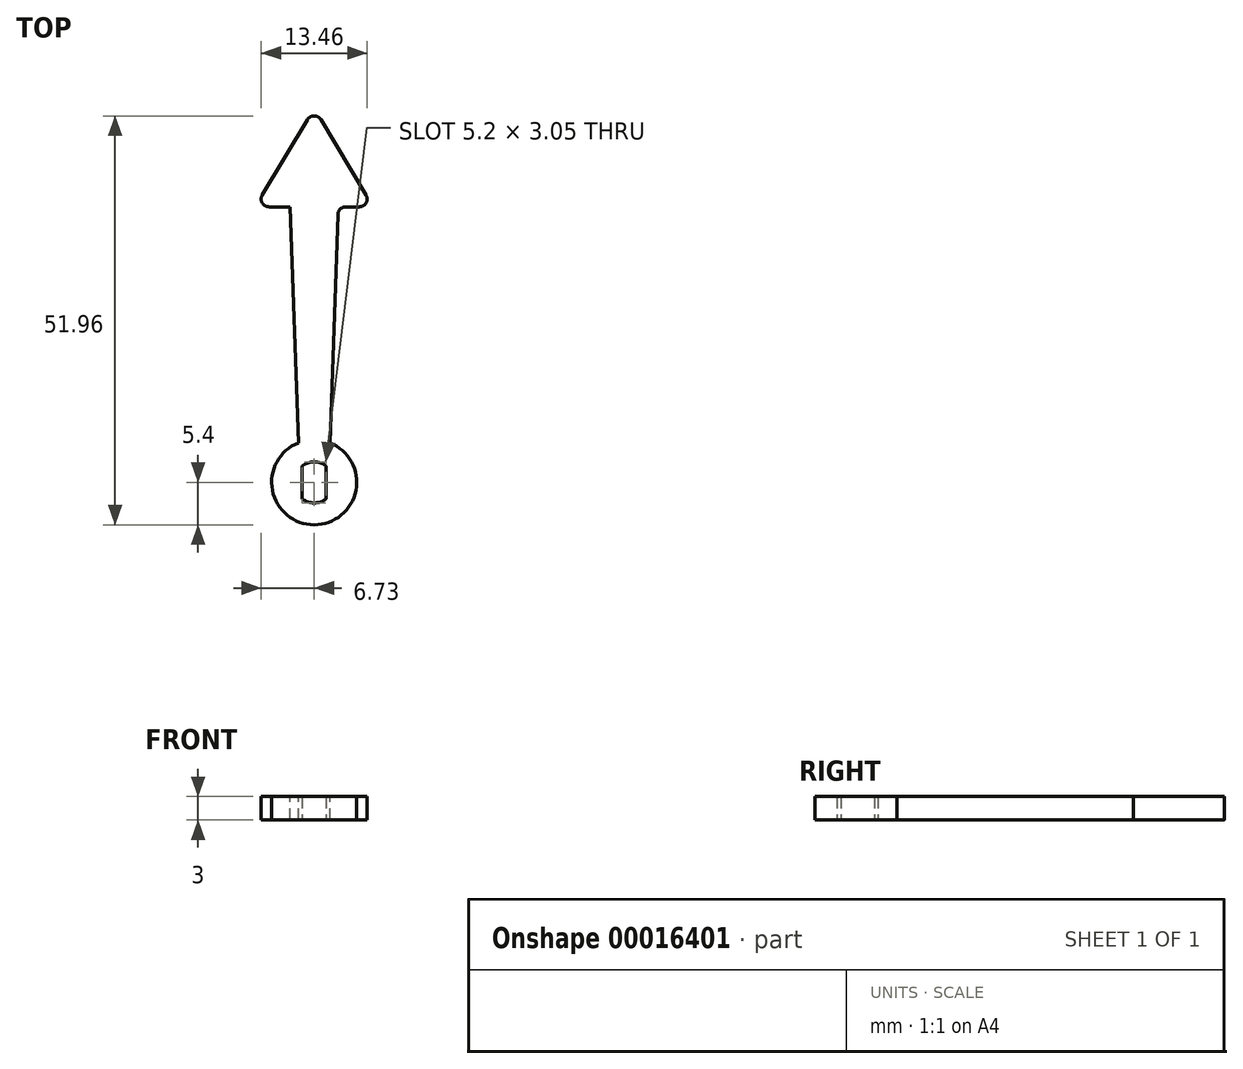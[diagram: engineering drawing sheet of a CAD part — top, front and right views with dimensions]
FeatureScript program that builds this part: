
annotation { "Feature Type Name" : "Feature", "Feature Type Description" : "" }
export const myFeature = defineFeature(function(context is Context, id is Id, definition is map)
    precondition{}
    {
        {
            var Q0;
            Q0=qCreatedBy(makeId("Top.planeOp"),FACE);
            var sketch = newSketch(context, id + "F0", { "sketchPlane" : qUnion([Q0])});
            skCircle(sketch, "E0", {"center": v(0, 0) * mm, "radius": 5.4 * mm});
            skCircle(sketch, "E1", {"center": v(0, 0) * mm, "radius": 2.6 * mm});
            skLineSegment(sketch, "E2", {"start": v(-1.53, 2.1) * mm, "end": v(-1.52, -2.1) * mm});
            skLineSegment(sketch, "E3", {"start": v(1.52, 2.1) * mm, "end": v(1.53, -2.1) * mm});
            skSolve(sketch);
        }
        {
            var Q0;
            Q0 = qSketchRegion(id + "F0", true);
            var Q1;
            {var subQ0=sQuery(id+"F0.wireOp",EDGE,"E3");Q1=makeQuery(id+"F0.imprint","IMPRINT",FACE,{"disambiguationData":[TD([[makeQuery(id+"F0.imprint","IMPRINT",EDGE,{"derivedFrom":subQ0}),1.0]])]});}
            var Q2;
            {var subQ0=sQuery(id+"F0.wireOp",EDGE,"E2");Q2=makeQuery(id+"F0.imprint","IMPRINT",FACE,{"disambiguationData":[TD([[makeQuery(id+"F0.imprint","IMPRINT",EDGE,{"derivedFrom":subQ0}),-1.0]])]});}
            extrude(context, id + "F1", {"entities" : qUnion([Q0, Q1, Q2]), "endBound" : BoundingType.SYMMETRIC, "depth" : 3 * mm});
        }
        {
            var Q0;
            Q0=makeQuery(id+"F1.opExtrude","CAP_FACE",FACE,{"disambiguationData":[OSD([sQuery(id+"F0.wireOp",EDGE,"0dc37ae7-439b-4512-b14e-6b0669575397"),sQuery(id+"F0.wireOp",EDGE,"E0"),sQuery(id+"F0.wireOp",EDGE,"48a892c1-0b3d-49af-834a-82fde92222b2"),sQuery(id+"F0.wireOp",EDGE,"72ea963c-e453-471c-a4fc-8eb423260cf1"),sQuery(id+"F0.wireOp",EDGE,"0ad86a4b-ed37-49b1-82e4-c23b011ab9ce.trimOffspring")])],"isStart":false});
            var sketch = newSketch(context, id + "F2", { "sketchPlane" : qUnion([Q0])});
            skLineSegment(sketch, "E4", {"start": v(0, 0) * mm, "end": v(0, 35) * mm, "construction": true});
            skLineSegment(sketch, "E5", {"start": v(-3.05, 35) * mm, "end": v(3.05, 35) * mm});
            skLineSegment(sketch, "E6", {"start": v(-2, 5.02) * mm, "end": v(2, 5.02) * mm});
            skLineSegment(sketch, "E7", {"start": v(3.05, 35) * mm, "end": v(2, 5.02) * mm});
            skLineSegment(sketch, "E8", {"start": v(-3.05, 35) * mm, "end": v(-2, 5.02) * mm});
            skSolve(sketch);
        }
        {
            var Q0;
            Q0 = qSketchRegion(id + "F2", true);
            var Q1;
            Q1=makeQuery(id+"F1.opExtrude","CAP_FACE",FACE,{"disambiguationData":[OSD([sQuery(id+"F0.wireOp",EDGE,"0dc37ae7-439b-4512-b14e-6b0669575397"),sQuery(id+"F0.wireOp",EDGE,"E0"),sQuery(id+"F0.wireOp",EDGE,"48a892c1-0b3d-49af-834a-82fde92222b2"),sQuery(id+"F0.wireOp",EDGE,"72ea963c-e453-471c-a4fc-8eb423260cf1"),sQuery(id+"F0.wireOp",EDGE,"0ad86a4b-ed37-49b1-82e4-c23b011ab9ce.trimOffspring")])],"isStart":true});
            extrude(context, id + "F3", {"entities" : qUnion([Q0]), "operationType" : NewBodyOperationType.ADD, "endBound" : BoundingType.UP_TO_SURFACE, "oppositeDirection" : true, "endBoundEntityFace" : qUnion([Q1]), "depth" : 25 * mm});
        }
        {
            var Q0;
            Q0=makeQuery(id+"F3.boolean.opBoolean","MERGE",FACE,{"derivedFrom":[makeQuery(id+"F1.opExtrude","CAP_FACE",FACE,{"disambiguationData":[OSD([sQuery(id+"F0.wireOp",EDGE,"0dc37ae7-439b-4512-b14e-6b0669575397"),sQuery(id+"F0.wireOp",EDGE,"E0"),sQuery(id+"F0.wireOp",EDGE,"48a892c1-0b3d-49af-834a-82fde92222b2"),sQuery(id+"F0.wireOp",EDGE,"72ea963c-e453-471c-a4fc-8eb423260cf1"),sQuery(id+"F0.wireOp",EDGE,"0ad86a4b-ed37-49b1-82e4-c23b011ab9ce.trimOffspring")])],"isStart":false}),makeQuery(id+"F3.opExtrude","CAP_FACE",FACE,{"disambiguationData":[OSD([sQuery(id+"F2.wireOp",EDGE,"E5"),sQuery(id+"F2.wireOp",EDGE,"E6"),sQuery(id+"F2.wireOp",EDGE,"E7"),sQuery(id+"F2.wireOp",EDGE,"E8")])],"isStart":true})]});
            var sketch = newSketch(context, id + "F4", { "sketchPlane" : qUnion([Q0])});
            skLineSegment(sketch, "E9", {"start": v(0, 35) * mm, "end": v(0, 47.5) * mm, "construction": true});
            skLineSegment(sketch, "E10", {"start": v(-7.5, 35) * mm, "end": v(7.5, 35) * mm});
            skLineSegment(sketch, "E11", {"start": v(0, 47.5) * mm, "end": v(-7.5, 35) * mm});
            skLineSegment(sketch, "E12", {"start": v(0, 47.5) * mm, "end": v(7.5, 35) * mm});
            skSolve(sketch);
        }
        {
            var Q0;
            Q0 = qSketchRegion(id + "F4", true);
            var Q1;
            Q1=makeQuery(id+"F3.boolean.opBoolean","MERGE",FACE,{"derivedFrom":[makeQuery(id+"F1.opExtrude","CAP_FACE",FACE,{"disambiguationData":[OSD([sQuery(id+"F0.wireOp",EDGE,"0dc37ae7-439b-4512-b14e-6b0669575397"),sQuery(id+"F0.wireOp",EDGE,"E0"),sQuery(id+"F0.wireOp",EDGE,"48a892c1-0b3d-49af-834a-82fde92222b2"),sQuery(id+"F0.wireOp",EDGE,"72ea963c-e453-471c-a4fc-8eb423260cf1"),sQuery(id+"F0.wireOp",EDGE,"0ad86a4b-ed37-49b1-82e4-c23b011ab9ce.trimOffspring")])],"isStart":true}),makeQuery(id+"F3.opExtrude","CAP_FACE",FACE,{"disambiguationData":[OSD([sQuery(id+"F2.wireOp",EDGE,"E5"),sQuery(id+"F2.wireOp",EDGE,"E6"),sQuery(id+"F2.wireOp",EDGE,"E7"),sQuery(id+"F2.wireOp",EDGE,"E8")])],"isStart":false})]});
            extrude(context, id + "F5", {"entities" : qUnion([Q0]), "operationType" : NewBodyOperationType.ADD, "endBound" : BoundingType.UP_TO_SURFACE, "oppositeDirection" : true, "endBoundEntityFace" : qUnion([Q1]), "depth" : 25 * mm});
        }
        {
            var Q0;
            Q0=makeQuery(id+"F5.opExtrude","SWEPT_EDGE",EDGE,{"disambiguationData":[OSD([sQuery(id+"F4.wireOp",EDGE,"E11"),sQuery(id+"F4.wireOp",EDGE,"E12")])]});
            var Q1;
            Q1=makeQuery(id+"F5.opExtrude","SWEPT_EDGE",EDGE,{"disambiguationData":[OSD([sQuery(id+"F4.wireOp",EDGE,"E10"),sQuery(id+"F4.wireOp",EDGE,"E12")])]});
            var Q2;
            Q2=makeQuery(id+"F5.opExtrude","SWEPT_EDGE",EDGE,{"disambiguationData":[OSD([sQuery(id+"F4.wireOp",EDGE,"E10"),sQuery(id+"F4.wireOp",EDGE,"E11")])]});
            var Q3;
            Q3=makeQuery(id+"F3.opExtrude","SWEPT_EDGE",EDGE,{"disambiguationData":[OSD([sQuery(id+"F2.wireOp",EDGE,"E5"),sQuery(id+"F2.wireOp",EDGE,"E8")])]});
            var Q4;
            Q4=makeQuery(id+"F3.opExtrude","SWEPT_EDGE",EDGE,{"disambiguationData":[OSD([sQuery(id+"F2.wireOp",EDGE,"E5"),sQuery(id+"F2.wireOp",EDGE,"E7")])]});
            fillet(context, id + "F6", {"entities" : qUnion([Q0, Q1, Q2, Q3, Q4]), "radius" : 1 * mm, "tangentPropagation" : true, "allowEdgeOverflow" : false});
        }
    });
